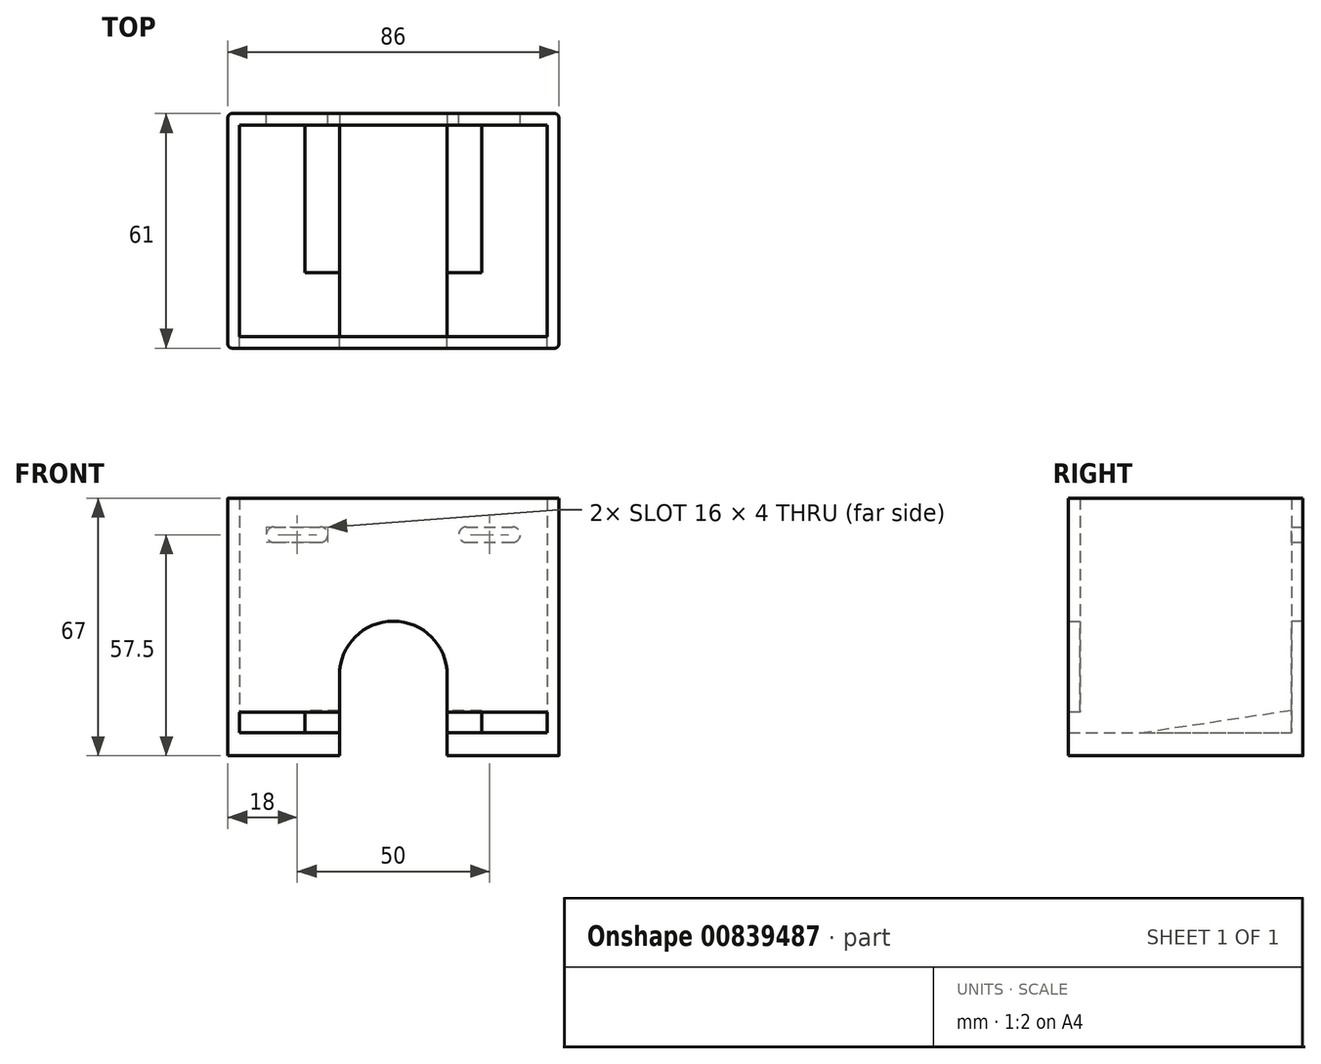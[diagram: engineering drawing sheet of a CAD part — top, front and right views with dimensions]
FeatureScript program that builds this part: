
annotation { "Feature Type Name" : "Feature", "Feature Type Description" : "" }
export const myFeature = defineFeature(function(context is Context, id is Id, definition is map)
    precondition{}
    {
        {
            var Q0;
            Q0=qCreatedBy(makeId("Top.planeOp"),FACE);
            var sketch = newSketch(context, id + "F0", { "sketchPlane" : qUnion([Q0])});
            skLineSegment(sketch, "E0.bottom", {"start": v(40, -27.5) * mm, "end": v(-40, -27.5) * mm});
            skLineSegment(sketch, "E0.top", {"start": v(40, 27.5) * mm, "end": v(-40, 27.5) * mm});
            skLineSegment(sketch, "E0.left", {"start": v(40, -27.5) * mm, "end": v(40, 27.5) * mm});
            skLineSegment(sketch, "E0.right", {"start": v(-40, -27.5) * mm, "end": v(-40, 27.5) * mm});
            skPoint(sketch, "E0.middle", {"position": v(0, 0) * mm});
            skLineSegment(sketch, "E1.bottom", {"start": v(43, -30.5) * mm, "end": v(-43, -30.5) * mm});
            skLineSegment(sketch, "E1.top", {"start": v(43, 30.5) * mm, "end": v(-43, 30.5) * mm});
            skLineSegment(sketch, "E1.left", {"start": v(43, -30.5) * mm, "end": v(43, 30.5) * mm});
            skLineSegment(sketch, "E1.right", {"start": v(-43, -30.5) * mm, "end": v(-43, 30.5) * mm});
            skSolve(sketch);
        }
        {
            var Q0;
            Q0=makeQuery(id+"F0.imprint","IMPRINT",FACE,{"disambiguationData":[TD([[makeQuery(id+"F0.imprint","IMPRINT",EDGE,{"derivedFrom":sQuery(id+"F0.wireOp",EDGE,"E0.bottom")}),1.0]])]});
            extrude(context, id + "F1", {"entities" : qUnion([Q0]), "depth" : 67 * mm, "offsetDistance" : 25 * mm});
        }
        {
            var Q0;
            Q0=makeQuery(id+"F0.imprint","IMPRINT",FACE,{"disambiguationData":[TD([[makeQuery(id+"F0.imprint","IMPRINT",EDGE,{"derivedFrom":sQuery(id+"F0.wireOp",EDGE,"E0.bottom")}),-1.0]])]});
            extrude(context, id + "F2", {"entities" : qUnion([Q0]), "operationType" : NewBodyOperationType.ADD, "depth" : 6 * mm, "offsetDistance" : 25 * mm});
        }
        {
            var Q0;
            Q0=makeQuery(id+"F1.opExtrude","SWEPT_FACE",FACE,{"disambiguationData":[OSD([sQuery(id+"F0.wireOp",EDGE,"E1.bottom")])]});
            var sketch = newSketch(context, id + "F3", { "sketchPlane" : qUnion([Q0])});
            skLineSegment(sketch, "E2.bottom", {"start": v(-43, 0) * mm, "end": v(43, 0) * mm});
            skLineSegment(sketch, "E2.top", {"start": v(-43, 6) * mm, "end": v(43, 6) * mm});
            skLineSegment(sketch, "E2.left", {"start": v(-43, 0) * mm, "end": v(-43, 6) * mm});
            skLineSegment(sketch, "E2.right", {"start": v(43, 0) * mm, "end": v(43, 6) * mm});
            skLineSegment(sketch, "E3.top", {"start": v(-43, 11.4) * mm, "end": v(43, 11.4) * mm});
            skLineSegment(sketch, "E3.left", {"start": v(-43, 6) * mm, "end": v(-43, 11.4) * mm});
            skLineSegment(sketch, "E3.right", {"start": v(43, 6) * mm, "end": v(43, 11.4) * mm});
            skLineSegment(sketch, "E4.bottom", {"start": v(-43, 11.4) * mm, "end": v(-40, 11.4) * mm});
            skLineSegment(sketch, "E4.top", {"start": v(-43, 6) * mm, "end": v(-40, 6) * mm});
            skLineSegment(sketch, "E4.left", {"start": v(-43, 11.4) * mm, "end": v(-43, 6) * mm});
            skLineSegment(sketch, "E4.right", {"start": v(-40, 11.4) * mm, "end": v(-40, 6) * mm});
            skLineSegment(sketch, "E5.bottom", {"start": v(43, 11.4) * mm, "end": v(40, 11.4) * mm});
            skLineSegment(sketch, "E5.top", {"start": v(43, 6) * mm, "end": v(40, 6) * mm});
            skLineSegment(sketch, "E5.left", {"start": v(43, 11.4) * mm, "end": v(43, 6) * mm});
            skLineSegment(sketch, "E5.right", {"start": v(40, 11.4) * mm, "end": v(40, 6) * mm});
            skSolve(sketch);
        }
        {
            var Q0;
            {var subQ0=sQuery(id+"F3.wireOp",EDGE,"E4.right");Q0=makeQuery(id+"F3.imprint","IMPRINT",FACE,{"disambiguationData":[TD([[makeQuery(id+"F3.imprint","IMPRINT",EDGE,{"derivedFrom":subQ0}),1.0]])]});}
            extrude(context, id + "F4", {"entities" : qUnion([Q0]), "operationType" : NewBodyOperationType.REMOVE, "oppositeDirection" : true, "depth" : 3 * mm, "offsetDistance" : 25 * mm});
        }
        {
            var Q0;
            Q0=qCreatedBy(makeId("Right.planeOp"),FACE);
            var sketch = newSketch(context, id + "F5", { "sketchPlane" : qUnion([Q0])});
            skLineSegment(sketch, "E6.bottom", {"start": v(29.14, 0) * mm, "end": v(-10.86, 0) * mm});
            skLineSegment(sketch, "E6.top", {"start": v(29.14, 12) * mm, "end": v(-10.86, 12) * mm});
            skLineSegment(sketch, "E6.left", {"start": v(29.14, 0) * mm, "end": v(29.14, 12) * mm});
            skLineSegment(sketch, "E6.right", {"start": v(-10.86, 0) * mm, "end": v(-10.86, 12) * mm});
            skLineSegment(sketch, "E7", {"start": v(-10.86, 0) * mm, "end": v(-10.86, 6) * mm});
            skLineSegment(sketch, "E8", {"start": v(-10.86, 6) * mm, "end": v(29.14, 12) * mm});
            skSolve(sketch);
        }
        {
            var Q0;
            Q0=makeQuery(id+"F0.imprint","IMPRINT",FACE,{"disambiguationData":[TD([[makeQuery(id+"F0.imprint","IMPRINT",EDGE,{"derivedFrom":sQuery(id+"F0.wireOp",EDGE,"E0.bottom")}),-1.0]])]});
            var sketch = newSketch(context, id + "F6", { "sketchPlane" : qUnion([Q0])});
            skLineSegment(sketch, "E9.bottom", {"start": v(14, 30.5) * mm, "end": v(-14, 30.5) * mm});
            skLineSegment(sketch, "E9.top", {"start": v(14, -30.5) * mm, "end": v(-14, -30.5) * mm});
            skLineSegment(sketch, "E9.left", {"start": v(14, 30.5) * mm, "end": v(14, -30.5) * mm});
            skLineSegment(sketch, "E9.right", {"start": v(-14, 30.5) * mm, "end": v(-14, -30.5) * mm});
            skPoint(sketch, "E9.middle", {"position": v(0, 0) * mm});
            skSolve(sketch);
        }
        {
            var Q0;
            {var subQ0=sQuery(id+"F6.wireOp",EDGE,"E9.top");Q0=makeQuery(id+"F6.imprint","IMPRINT",FACE,{"disambiguationData":[TD([[makeQuery(id+"F6.imprint","IMPRINT",EDGE,{"derivedFrom":subQ0}),-1.0]])]});}
            var Q1;
            {var subQ0=sQuery(id+"F6.wireOp",EDGE,"E9.left");var subQ1=makeQuery(id+"F0.imprint","IMPRINT",EDGE,{"derivedFrom":sQuery(id+"F0.wireOp",EDGE,"E0.top")});var subQ2=makeQuery(id+"F6.imprint","INTERSECT",VERTEX,{"derivedFrom":[subQ1,subQ0]});Q1=makeQuery(id+"F6.imprint","IMPRINT",FACE,{"disambiguationData":[TD([[makeQuery(id+"F6.imprint","IMPRINT",EDGE,{"disambiguationData":[TD([[subQ2,-1.0]])],"derivedFrom":subQ0}),-1.0]])]});}
            var Q2;
            {var subQ0=sQuery(id+"F6.wireOp",EDGE,"E9.bottom");Q2=makeQuery(id+"F6.imprint","IMPRINT",FACE,{"disambiguationData":[TD([[makeQuery(id+"F6.imprint","IMPRINT",EDGE,{"derivedFrom":subQ0}),1.0]])]});}
            extrude(context, id + "F7", {"entities" : qUnion([Q0, Q1, Q2]), "operationType" : NewBodyOperationType.REMOVE, "depth" : 35 * mm, "offsetDistance" : 25 * mm});
        }
        {
            var Q0;
            {var subQ0=sQuery(id+"F6.wireOp",EDGE,"E9.left");Q0=makeQuery(id+"F7.boolean.opBoolean","COPY",EDGE,{"disambiguationData":[TD([makeQuery(id+"F1.opExtrude","SWEPT_FACE",FACE,{"disambiguationData":[OSD([sQuery(id+"F0.wireOp",EDGE,"E0.bottom")])]})])],"derivedFrom":makeQuery(id+"F7.opExtrude","CAP_EDGE",EDGE,{"disambiguationData":[OSD([subQ0])],"isStart":false})});}
            var Q1;
            {var subQ0=sQuery(id+"F6.wireOp",EDGE,"E9.right");Q1=makeQuery(id+"F7.boolean.opBoolean","COPY",EDGE,{"disambiguationData":[TD([makeQuery(id+"F1.opExtrude","SWEPT_FACE",FACE,{"disambiguationData":[OSD([sQuery(id+"F0.wireOp",EDGE,"E0.bottom")])]})])],"derivedFrom":makeQuery(id+"F7.opExtrude","CAP_EDGE",EDGE,{"disambiguationData":[OSD([subQ0])],"isStart":false})});}
            var Q2;
            {var subQ0=sQuery(id+"F6.wireOp",EDGE,"E9.right");Q2=makeQuery(id+"F7.boolean.opBoolean","COPY",EDGE,{"disambiguationData":[TD([makeQuery(id+"F1.opExtrude","SWEPT_FACE",FACE,{"disambiguationData":[OSD([sQuery(id+"F0.wireOp",EDGE,"E0.top")])]})])],"derivedFrom":makeQuery(id+"F7.opExtrude","CAP_EDGE",EDGE,{"disambiguationData":[OSD([subQ0])],"isStart":false})});}
            var Q3;
            {var subQ0=sQuery(id+"F6.wireOp",EDGE,"E9.left");Q3=makeQuery(id+"F7.boolean.opBoolean","COPY",EDGE,{"disambiguationData":[TD([makeQuery(id+"F1.opExtrude","SWEPT_FACE",FACE,{"disambiguationData":[OSD([sQuery(id+"F0.wireOp",EDGE,"E0.top")])]})])],"derivedFrom":makeQuery(id+"F7.opExtrude","CAP_EDGE",EDGE,{"disambiguationData":[OSD([subQ0])],"isStart":false})});}
            fillet(context, id + "F8", {"entities" : qUnion([Q0, Q1, Q2, Q3]), "radius" : 14 * mm, "tangentPropagation" : true, "allowEdgeOverflow" : false});
        }
        {
            var Q0;
            {var subQ0=sQuery(id+"F5.wireOp",EDGE,"E6.bottom");Q0=makeQuery(id+"F5.imprint","IMPRINT",FACE,{"disambiguationData":[TD([[makeQuery(id+"F5.imprint","IMPRINT",EDGE,{"derivedFrom":subQ0}),-1.0]])]});}
            extrude(context, id + "F9", {"entities" : qUnion([Q0]), "operationType" : NewBodyOperationType.ADD, "depth" : 46 * mm, "offsetDistance" : 25 * mm, "symmetric" : true});
        }
        {
            var Q0;
            Q0=makeQuery(id+"F9.opExtrude","SWEPT_FACE",FACE,{"disambiguationData":[OSD([sQuery(id+"F5.wireOp",EDGE,"E8")])]});
            var sketch = newSketch(context, id + "F10", { "sketchPlane" : qUnion([Q0])});
            skLineSegment(sketch, "E10.bottom", {"start": v(14, -39.33) * mm, "end": v(-14, -39.33) * mm});
            skLineSegment(sketch, "E10.top", {"start": v(14, 37.55) * mm, "end": v(-14, 37.55) * mm});
            skLineSegment(sketch, "E10.left", {"start": v(14, -39.33) * mm, "end": v(14, 37.55) * mm});
            skLineSegment(sketch, "E10.right", {"start": v(-14, -39.33) * mm, "end": v(-14, 37.55) * mm});
            skPoint(sketch, "E10.middle", {"position": v(0, -0.9) * mm});
            skSolve(sketch);
        }
        {
            var Q0;
            {var subQ1=sQuery(id+"F5.wireOp",EDGE,"E8");var subQ7=sQuery(id+"F5.wireOp",EDGE,"E6.left");var subQ8=makeQuery(id+"F9.opExtrude","SWEPT_EDGE",EDGE,{"disambiguationData":[OSD([sQuery(id+"F5.wireOp",EDGE,"E6.top"),subQ7,subQ1])]});Q0=makeQuery(id+"F10.imprint","IMPRINT",FACE,{"disambiguationData":[TD([[makeQuery(id+"F10.imprint","IMPRINT",EDGE,{"derivedFrom":subQ8}),1.0]])]});}
            var Q1;
            {var subQ0=sQuery(id+"F10.wireOp",EDGE,"E10.bottom");Q1=makeQuery(id+"F10.imprint","IMPRINT",FACE,{"disambiguationData":[TD([[makeQuery(id+"F10.imprint","IMPRINT",EDGE,{"derivedFrom":subQ0}),-1.0]])]});}
            extrude(context, id + "F11", {"entities" : qUnion([Q0, Q1]), "operationType" : NewBodyOperationType.REMOVE, "oppositeDirection" : true, "depth" : 25 * mm, "offsetDistance" : 25 * mm});
        }
        {
            var Q0;
            Q0=makeQuery(id+"F1.opExtrude","SWEPT_FACE",FACE,{"disambiguationData":[OSD([sQuery(id+"F0.wireOp",EDGE,"E1.top")])]});
            var sketch = newSketch(context, id + "F12", { "sketchPlane" : qUnion([Q0])});
            skLineSegment(sketch, "E11.bottom", {"start": v(25, 57.5) * mm, "end": v(-25, 57.5) * mm});
            skLineSegment(sketch, "E11.top", {"start": v(25, -57.5) * mm, "end": v(-25, -57.5) * mm});
            skLineSegment(sketch, "E11.left", {"start": v(25, 57.5) * mm, "end": v(25, -57.5) * mm});
            skLineSegment(sketch, "E11.right", {"start": v(-25, 57.5) * mm, "end": v(-25, -57.5) * mm});
            skPoint(sketch, "E11.middle", {"position": v(0, 0) * mm});
            skLineSegment(sketch, "E12.bottom", {"start": v(-19, 55.5) * mm, "end": v(-31, 55.5) * mm});
            skLineSegment(sketch, "E12.top", {"start": v(-19, 59.5) * mm, "end": v(-31, 59.5) * mm});
            skLineSegment(sketch, "E12.left", {"start": v(-19, 55.5) * mm, "end": v(-19, 59.5) * mm});
            skLineSegment(sketch, "E12.right", {"start": v(-31, 55.5) * mm, "end": v(-31, 59.5) * mm});
            skPoint(sketch, "E12.middle", {"position": v(-25, 57.5) * mm});
            skLineSegment(sketch, "E13.bottom", {"start": v(31, 55.5) * mm, "end": v(19, 55.5) * mm});
            skLineSegment(sketch, "E13.top", {"start": v(31, 59.5) * mm, "end": v(19, 59.5) * mm});
            skLineSegment(sketch, "E13.left", {"start": v(31, 55.5) * mm, "end": v(31, 59.5) * mm});
            skLineSegment(sketch, "E13.right", {"start": v(19, 55.5) * mm, "end": v(19, 59.5) * mm});
            skPoint(sketch, "E13.middle", {"position": v(25, 57.5) * mm});
            skArc(sketch, "E14", {"start": v(-31, 59.5) * mm, "mid": v(-33, 57.5) * mm, "end": v(-31, 55.5) * mm});
            skArc(sketch, "E15", {"start": v(-19, 55.5) * mm, "mid": v(-17, 57.5) * mm, "end": v(-19, 59.5) * mm});
            skArc(sketch, "E16", {"start": v(19, 59.5) * mm, "mid": v(17, 57.5) * mm, "end": v(19, 55.5) * mm});
            skArc(sketch, "E17", {"start": v(31, 55.5) * mm, "mid": v(33, 57.5) * mm, "end": v(31, 59.5) * mm});
            skSolve(sketch);
        }
        {
            var Q0;
            Q0=makeQuery(id+"F12.imprint","IMPRINT",FACE,{"disambiguationData":[TD([[makeQuery(id+"F12.imprint","IMPRINT",EDGE,{"derivedFrom":sQuery(id+"F12.wireOp",EDGE,"E12.right")}),1.0]])]});
            var Q1;
            {var subQ4=sQuery(id+"F12.wireOp",EDGE,"E12.top");Q1=makeQuery(id+"F12.imprint","IMPRINT",FACE,{"disambiguationData":[TD([[makeQuery(id+"F12.imprint","IMPRINT",EDGE,{"derivedFrom":subQ4}),1.0]])]});}
            var Q2;
            {var subQ0=sQuery(id+"F12.wireOp",EDGE,"E11.right");var subQ1=sQuery(id+"F12.wireOp",EDGE,"E11.bottom");var subQ2=makeQuery(id+"F12.imprint","INTERSECT",VERTEX,{"derivedFrom":[subQ1,subQ0]});Q2=makeQuery(id+"F12.imprint","IMPRINT",FACE,{"disambiguationData":[TD([[makeQuery(id+"F12.imprint","IMPRINT",EDGE,{"disambiguationData":[TD([[subQ2,1.0]])],"derivedFrom":subQ1}),1.0]])]});}
            var Q3;
            {var subQ0=sQuery(id+"F12.wireOp",EDGE,"E15");var subQ1=sQuery(id+"F12.wireOp",EDGE,"E11.bottom");var subQ2=makeQuery(id+"F12.imprint","INTERSECT",VERTEX,{"derivedFrom":[subQ1,subQ0]});Q3=makeQuery(id+"F12.imprint","IMPRINT",FACE,{"disambiguationData":[TD([[makeQuery(id+"F12.imprint","IMPRINT",EDGE,{"disambiguationData":[TD([[subQ2,-1.0]])],"derivedFrom":subQ1}),1.0]])]});}
            var Q4;
            {var subQ0=sQuery(id+"F12.wireOp",EDGE,"E15");var subQ1=sQuery(id+"F12.wireOp",EDGE,"E11.bottom");var subQ2=makeQuery(id+"F12.imprint","INTERSECT",VERTEX,{"derivedFrom":[subQ1,subQ0]});Q4=makeQuery(id+"F12.imprint","IMPRINT",FACE,{"disambiguationData":[TD([[makeQuery(id+"F12.imprint","IMPRINT",EDGE,{"disambiguationData":[TD([[subQ2,-1.0]])],"derivedFrom":subQ1}),-1.0]])]});}
            var Q5;
            {var subQ0=sQuery(id+"F12.wireOp",EDGE,"E13.right");var subQ1=sQuery(id+"F12.wireOp",EDGE,"E11.bottom");var subQ2=makeQuery(id+"F12.imprint","INTERSECT",VERTEX,{"derivedFrom":[subQ1,subQ0]});Q5=makeQuery(id+"F12.imprint","IMPRINT",FACE,{"disambiguationData":[TD([[makeQuery(id+"F12.imprint","IMPRINT",EDGE,{"disambiguationData":[TD([[subQ2,-1.0]])],"derivedFrom":subQ1}),1.0]])]});}
            var Q6;
            {var subQ0=sQuery(id+"F12.wireOp",EDGE,"E13.right");var subQ1=sQuery(id+"F12.wireOp",EDGE,"E11.bottom");var subQ2=makeQuery(id+"F12.imprint","INTERSECT",VERTEX,{"derivedFrom":[subQ1,subQ0]});Q6=makeQuery(id+"F12.imprint","IMPRINT",FACE,{"disambiguationData":[TD([[makeQuery(id+"F12.imprint","IMPRINT",EDGE,{"disambiguationData":[TD([[subQ2,-1.0]])],"derivedFrom":subQ1}),-1.0]])]});}
            var Q7;
            {var subQ6=sQuery(id+"F12.wireOp",EDGE,"E13.top");Q7=makeQuery(id+"F12.imprint","IMPRINT",FACE,{"disambiguationData":[TD([[makeQuery(id+"F12.imprint","IMPRINT",EDGE,{"derivedFrom":subQ6}),1.0]])]});}
            var Q8;
            {var subQ0=sQuery(id+"F12.wireOp",EDGE,"E11.left");var subQ1=sQuery(id+"F12.wireOp",EDGE,"E11.bottom");var subQ2=makeQuery(id+"F12.imprint","INTERSECT",VERTEX,{"derivedFrom":[subQ1,subQ0]});Q8=makeQuery(id+"F12.imprint","IMPRINT",FACE,{"disambiguationData":[TD([[makeQuery(id+"F12.imprint","IMPRINT",EDGE,{"disambiguationData":[TD([[subQ2,-1.0]])],"derivedFrom":subQ1}),1.0]])]});}
            var Q9;
            Q9=makeQuery(id+"F12.imprint","IMPRINT",FACE,{"disambiguationData":[TD([[makeQuery(id+"F12.imprint","IMPRINT",EDGE,{"derivedFrom":sQuery(id+"F12.wireOp",EDGE,"E13.left")}),-1.0]])]});
            extrude(context, id + "F13", {"entities" : qUnion([Q0, Q1, Q2, Q3, Q4, Q5, Q6, Q7, Q8, Q9]), "operationType" : NewBodyOperationType.REMOVE, "oppositeDirection" : true, "depth" : 6 * mm, "offsetDistance" : 25 * mm});
        }
        {
            var Q0;
            Q0=makeQuery(id+"F1.opExtrude","SWEPT_EDGE",EDGE,{"disambiguationData":[OSD([sQuery(id+"F0.wireOp",EDGE,"E1.bottom"),sQuery(id+"F0.wireOp",EDGE,"E1.right")])]});
            var Q1;
            Q1=makeQuery(id+"F1.opExtrude","SWEPT_EDGE",EDGE,{"disambiguationData":[OSD([sQuery(id+"F0.wireOp",EDGE,"E1.bottom"),sQuery(id+"F0.wireOp",EDGE,"E1.left")])]});
            var Q2;
            Q2=makeQuery(id+"F1.opExtrude","SWEPT_EDGE",EDGE,{"disambiguationData":[OSD([sQuery(id+"F0.wireOp",EDGE,"E1.top"),sQuery(id+"F0.wireOp",EDGE,"E1.left")])]});
            var Q3;
            Q3=makeQuery(id+"F1.opExtrude","SWEPT_EDGE",EDGE,{"disambiguationData":[OSD([sQuery(id+"F0.wireOp",EDGE,"E1.top"),sQuery(id+"F0.wireOp",EDGE,"E1.right")])]});
            fillet(context, id + "F14", {"entities" : qUnion([Q0, Q1, Q2, Q3]), "radius" : 1 * mm, "tangentPropagation" : true, "allowEdgeOverflow" : false});
        }
    });
